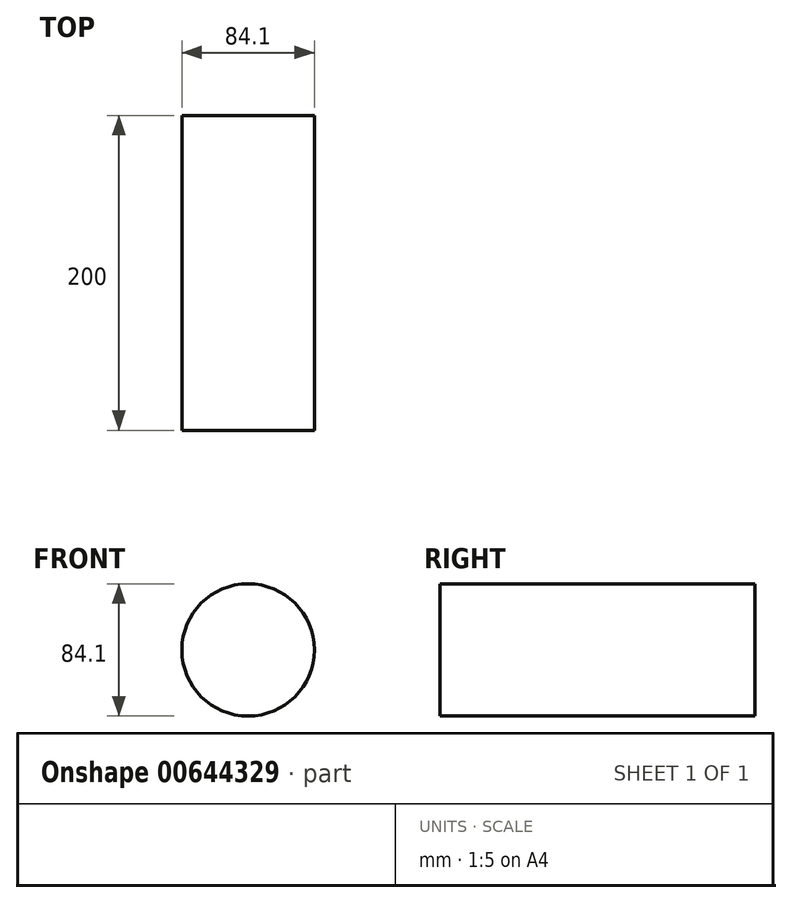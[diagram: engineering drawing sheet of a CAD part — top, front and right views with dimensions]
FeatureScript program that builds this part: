
annotation { "Feature Type Name" : "Feature", "Feature Type Description" : "" }
export const myFeature = defineFeature(function(context is Context, id is Id, definition is map)
    precondition{}
    {
        {
            var Q0;
            Q0=qCreatedBy(makeId("Front.planeOp"),FACE);
            var sketch = newSketch(context, id + "F0", { "sketchPlane" : qUnion([Q0])});
            skCircle(sketch, "E0", {"center": v(0, 0) * mm, "radius": 42.05 * mm});
            skCircle(sketch, "E1", {"center": v(0, 0) * mm, "radius": 33.57 * mm});
            skSolve(sketch);
        }
        {
            var Q0;
            Q0=sQuery(id+"F0.wireOp",EDGE,"E0");
            extrude(context, id + "F1", {"bodyType" : ToolBodyType.SURFACE, "surfaceEntities" : qUnion([Q0]), "depth" : 200 * mm, "offsetDistance" : 25 * mm});
        }
    });
